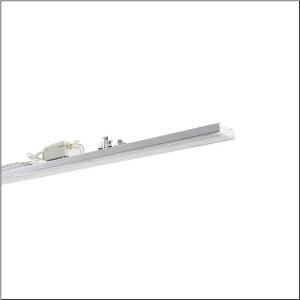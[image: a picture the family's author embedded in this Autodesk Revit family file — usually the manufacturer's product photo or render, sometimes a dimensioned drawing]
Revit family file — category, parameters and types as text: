
# Revit family: licross_r__21_recessed_mo_52tl19dn495g_9489
name_source: partatom
category: Lighting Fixtures
units: mm (PartAtom-declared; Revit-internal decimal feet)

## family parameters
Cut with Voids When Loaded = No
Host = Face
Light Source = No
Part Type = Normal
Room Calculation Point = No
Round Connector Dimension = Use Diameter
Shared = No

## types (1)
- --- (1 x LED, 9850 lm, 58 W, 4000K)
    Apparent Load = 58 VA
    CIE Flux Codes = 55 90 98 100 100
    Color Rendering = 80
    Color Temperature = 4000K
    Default Elevation = 1800 mm
    Description = Licross® 21 Recessed MO, luminaire insert, of sheet steel, galvanised, coil coated, white, length: 1.500mm, width: 66mm, height: 67mm, LED rated luminous flux: 9.850lm, light colour: 840, control gear: DALI 2, with plug, 5-pole, with phase selection, mains connection: 220..240V, AC, 50/60Hz, rated input power: 58W, halogen-free wiring, primary light control with lens, of plastic, primary optical cover: cover, of PMMA, light emission: direct distribution, primary light characteristic: double asymmetric, protection rating (complete): IP40, insulation class (complete): insulation class I (protective earthing), certification: CE, ENEC, VDE, UKCA, protection symbol: D if used in an environment without relevant dust loads with corresponding accessories, impact resistance: IK06, permissible ambient temperature for indoor applications: -25..+35°C, corresponds to IFS (International Featured Standards) requirements for safety and quality in the food industry, reducing of maximum allowable ambient temperature of 5°C with ceiling mounting, LABS conformity tested according to VDMA 24364:2018-05, packaging unit: 1 piece
    Height = 58 mm
    Lamp = 1 x LED
    Lamp Light Flux = 9850 lm
    Lamp Power = 58 W
    Lamp count = 1
    Length = 1500 mm
    Luminous efficacy = 170 lm/W
    Manufacturer = Siteco
    ModVariant = No
    Model = 52TL19DN495G
    Mounting Place = Ceiling
    Mounting Type = Pendant
    Number of Poles = 1
    OnlyDefault = Yes
    Power Factor = 1
    Product Name = Licross® 21 Recessed MO
    Product group = luminaire insert
    ProductGroupID = 901
    Protection Class = Protection class I
    Protection Degree = IP 40
    RLX_Detail_Level = 1
    RLX_Emergency_Light_Flux = 0 lm
    RLX_Emergency_Type = 0
    RLX_Emergency_Type_DB = No
    RlxData = <blob elided: 24577 chars, md5=d28d5075>
    Socket = socket
    Standby Power = 0 W
    System Light Flux = 9850 lm
    System Power = 58 W
    Type Comments = factory setting: luminous flux: 100 % | dim-lin: 254 | 390 mA
    Type Image = l_1296930.jpg
    URL = http://relux.com
    VarID = @adj_059577
    Voltage = 0 V
    Weight = 0.00 kg
    Width = 66 mm

## geometry (parser evidence)
native form markers: Blend x4, Sweep x12
no freeform markers — native parametric forms only
